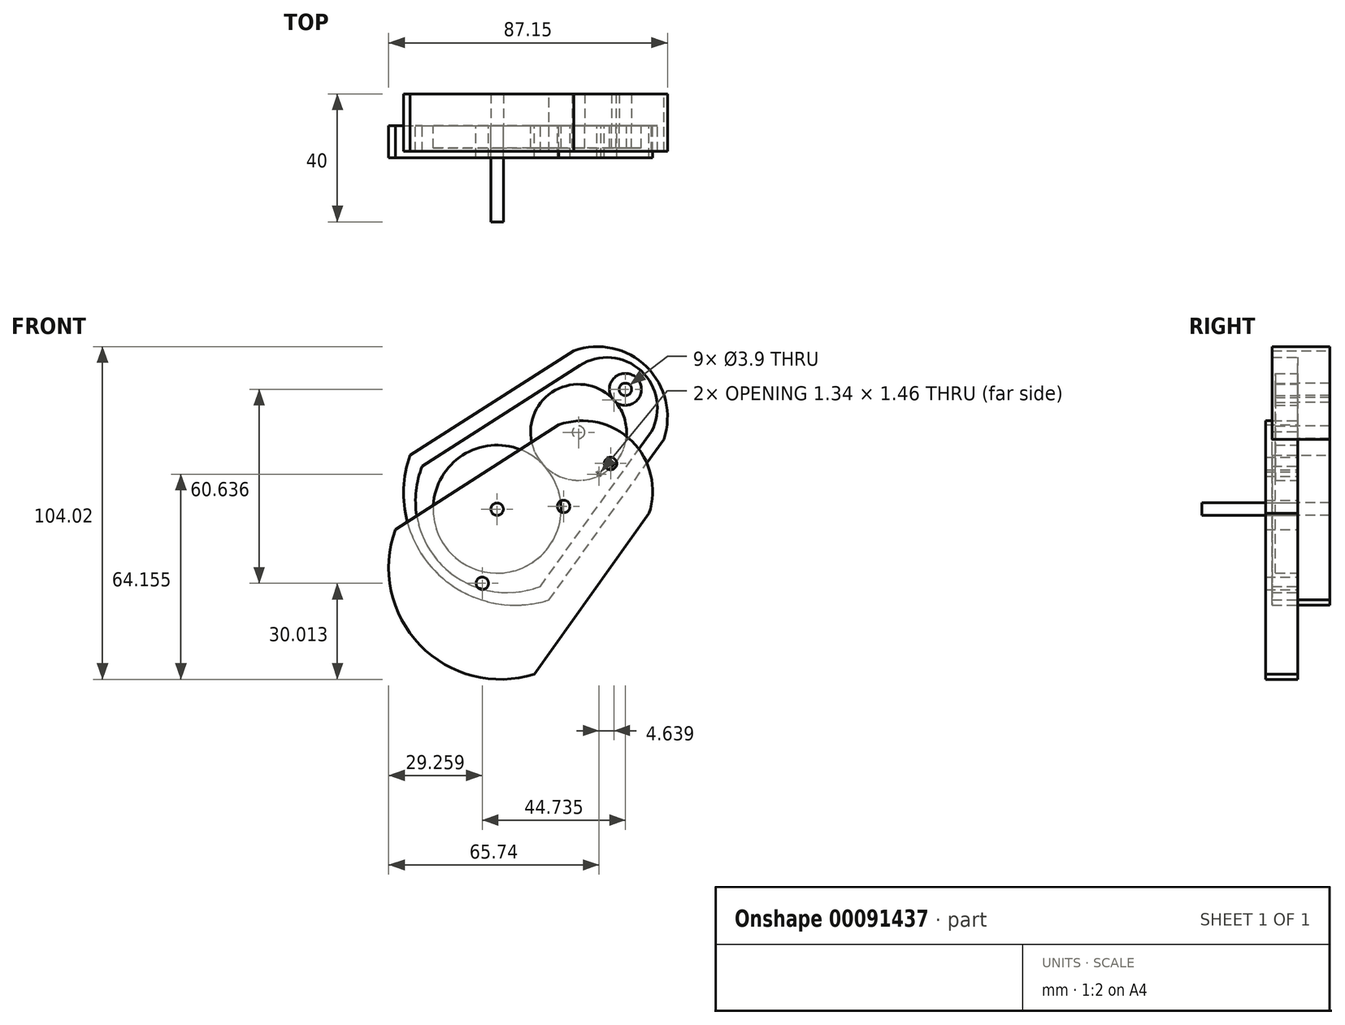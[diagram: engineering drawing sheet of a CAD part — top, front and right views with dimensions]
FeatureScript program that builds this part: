
annotation { "Feature Type Name" : "Feature", "Feature Type Description" : "" }
export const myFeature = defineFeature(function(context is Context, id is Id, definition is map)
    precondition{}
    {
        {
            var Q0;
            Q0=qCreatedBy(makeId("Front.planeOp"),FACE);
            var sketch = newSketch(context, id + "F0", { "sketchPlane" : qUnion([Q0])});
            skCircle(sketch, "E0", {"center": v(26.6, 43.79) * mm, "radius": 5 * mm});
            skCircle(sketch, "E1", {"center": v(11.94, 30.37) * mm, "radius": 15 * mm});
            skCircle(sketch, "E2", {"center": v(-13.5, 6.34) * mm, "radius": 20 * mm});
            skLineSegment(sketch, "E3", {"start": v(-36.89, 19.76) * mm, "end": v(12.3, 51.26) * mm});
            skLineSegment(sketch, "E4", {"start": v(0, -17.79) * mm, "end": v(34.74, 30.55) * mm});
            skArc(sketch, "E5", {"start": v(34.74, 30.55) * mm, "mid": v(31.52, 49.57) * mm, "end": v(12.3, 51.26) * mm});
            skArc(sketch, "E6", {"start": v(-36.89, 19.76) * mm, "mid": v(-30.8, -11.15) * mm, "end": v(0, -17.79) * mm});
            skCircle(sketch, "E7", {"center": v(-13.5, 6.34) * mm, "radius": 1.95 * mm});
            skCircle(sketch, "E8", {"center": v(11.94, 30.37) * mm, "radius": 1.95 * mm});
            skCircle(sketch, "E9", {"center": v(26.6, 43.79) * mm, "radius": 1.95 * mm});
            skLineSegment(sketch, "E10", {"start": v(-40.68, 23.15) * mm, "end": v(10.45, 55.9) * mm});
            skLineSegment(sketch, "E11", {"start": v(2.72, -22.05) * mm, "end": v(38.6, 28.17) * mm});
            skArc(sketch, "E12", {"start": v(38.6, 28.17) * mm, "mid": v(33.2, 50.84) * mm, "end": v(10.45, 55.9) * mm});
            skArc(sketch, "E13", {"start": v(-40.68, 23.15) * mm, "mid": v(-33.01, -12.93) * mm, "end": v(2.72, -22.05) * mm});
            skSolve(sketch);
        }
        {
            var Q0;
            Q0=makeQuery(id+"F0.imprint","IMPRINT",FACE,{"disambiguationData":[TD([[makeQuery(id+"F0.imprint","IMPRINT",EDGE,{"derivedFrom":sQuery(id+"F0.wireOp",EDGE,"E3")}),1.0]])]});
            extrude(context, id + "F1", {"entities" : qUnion([Q0]), "depth" : 8 * mm});
        }
        {
            var Q0;
            Q0 = qSketchRegion(id + "F0", true);
            var Q1;
            {var subQ0=sQuery(id+"F0.wireOp",EDGE,"E2");Q1=makeQuery(id+"F0.imprint","IMPRINT",FACE,{"disambiguationData":[TD([[makeQuery(id+"F0.imprint","IMPRINT",EDGE,{"derivedFrom":subQ0}),-1.0]])]});}
            var Q2;
            Q2=makeQuery(id+"F0.imprint","IMPRINT",FACE,{"disambiguationData":[TD([[makeQuery(id+"F0.imprint","IMPRINT",EDGE,{"derivedFrom":sQuery(id+"F0.wireOp",EDGE,"E8")}),-1.0]])]});
            var Q3;
            Q3=makeQuery(id+"F0.imprint","IMPRINT",FACE,{"disambiguationData":[TD([[makeQuery(id+"F0.imprint","IMPRINT",EDGE,{"derivedFrom":sQuery(id+"F0.wireOp",EDGE,"E2")}),1.0]])]});
            var Q4;
            Q4=makeQuery(id+"F0.imprint","IMPRINT",FACE,{"disambiguationData":[TD([[makeQuery(id+"F0.imprint","IMPRINT",EDGE,{"derivedFrom":sQuery(id+"F0.wireOp",EDGE,"E9")}),-1.0]])]});
            extrude(context, id + "F2", {"entities" : qUnion([Q0, Q1, Q2, Q3, Q4]), "operationType" : NewBodyOperationType.ADD, "oppositeDirection" : true, "depth" : 10 * mm});
        }
        {
            var Q0;
            Q0=qCreatedBy(makeId("Front.planeOp"),FACE);
            var sketch = newSketch(context, id + "F3", { "sketchPlane" : qUnion([Q0])});
            skCircle(sketch, "E14", {"center": v(21.95, 20.6) * mm, "radius": 5 * mm});
            skCircle(sketch, "E15", {"center": v(7.3, 7.18) * mm, "radius": 15 * mm});
            skCircle(sketch, "E16", {"center": v(-18.14, -16.85) * mm, "radius": 20 * mm});
            skLineSegment(sketch, "E17", {"start": v(-41.53, -3.43) * mm, "end": v(7.67, 28.08) * mm});
            skLineSegment(sketch, "E18", {"start": v(-4.64, -40.97) * mm, "end": v(30.1, 7.36) * mm});
            skArc(sketch, "E19", {"start": v(30.1, 7.36) * mm, "mid": v(26.88, 26.38) * mm, "end": v(7.67, 28.08) * mm});
            skArc(sketch, "E20", {"start": v(-41.53, -3.43) * mm, "mid": v(-35.44, -34.34) * mm, "end": v(-4.64, -40.97) * mm});
            skCircle(sketch, "E21", {"center": v(-18.14, -16.85) * mm, "radius": 1.95 * mm});
            skCircle(sketch, "E22", {"center": v(7.3, 7.18) * mm, "radius": 1.95 * mm});
            skCircle(sketch, "E23", {"center": v(21.95, 20.6) * mm, "radius": 1.95 * mm});
            skLineSegment(sketch, "E24", {"start": v(-45.32, -0.04) * mm, "end": v(5.81, 32.7) * mm});
            skLineSegment(sketch, "E25", {"start": v(-1.92, -45.24) * mm, "end": v(33.96, 4.99) * mm});
            skArc(sketch, "E26", {"start": v(33.96, 4.99) * mm, "mid": v(28.56, 27.66) * mm, "end": v(5.81, 32.7) * mm});
            skArc(sketch, "E27", {"start": v(-45.32, -0.04) * mm, "mid": v(-37.65, -36.11) * mm, "end": v(-1.92, -45.24) * mm});
            skSolve(sketch);
        }
        {
            var Q0;
            Q0=makeQuery(id+"F3.imprint","IMPRINT",FACE,{"disambiguationData":[TD([[makeQuery(id+"F3.imprint","IMPRINT",EDGE,{"derivedFrom":sQuery(id+"F3.wireOp",EDGE,"E17")}),1.0]])]});
            var Q1;
            {var subQ0=sQuery(id+"F3.wireOp",EDGE,"E16");Q1=makeQuery(id+"F3.imprint","IMPRINT",FACE,{"disambiguationData":[TD([[makeQuery(id+"F3.imprint","IMPRINT",EDGE,{"derivedFrom":subQ0}),-1.0]])]});}
            var Q2;
            Q2=makeQuery(id+"F3.imprint","IMPRINT",FACE,{"disambiguationData":[TD([[makeQuery(id+"F3.imprint","IMPRINT",EDGE,{"derivedFrom":sQuery(id+"F3.wireOp",EDGE,"E16")}),1.0]])]});
            var Q3;
            Q3=makeQuery(id+"F3.imprint","IMPRINT",FACE,{"disambiguationData":[TD([[makeQuery(id+"F3.imprint","IMPRINT",EDGE,{"derivedFrom":sQuery(id+"F3.wireOp",EDGE,"E22")}),-1.0]])]});
            var Q4;
            Q4=makeQuery(id+"F3.imprint","IMPRINT",FACE,{"disambiguationData":[TD([[makeQuery(id+"F3.imprint","IMPRINT",EDGE,{"derivedFrom":sQuery(id+"F3.wireOp",EDGE,"E23")}),-1.0]])]});
            extrude(context, id + "F4", {"entities" : qUnion([Q0, Q1, Q2, Q3, Q4]), "depth" : 10 * mm});
        }
        {
            var Q0;
            Q0=makeQuery(id+"F0.imprint","IMPRINT",FACE,{"disambiguationData":[TD([[makeQuery(id+"F0.imprint","IMPRINT",EDGE,{"derivedFrom":sQuery(id+"F0.wireOp",EDGE,"E7")}),1.0]])]});
            extrude(context, id + "F5", {"entities" : qUnion([Q0]), "depth" : 30 * mm});
        }
        {
            var Q0;
            Q0=makeQuery(id+"F0.imprint","IMPRINT",FACE,{"disambiguationData":[TD([[makeQuery(id+"F0.imprint","IMPRINT",EDGE,{"derivedFrom":sQuery(id+"F0.wireOp",EDGE,"E2")}),1.0]])]});
            extrude(context, id + "F6", {"entities" : qUnion([Q0]), "depth" : 7 * mm});
        }
        {
            var Q0;
            Q0=makeQuery(id+"F0.imprint","IMPRINT",FACE,{"disambiguationData":[TD([[makeQuery(id+"F0.imprint","IMPRINT",EDGE,{"derivedFrom":sQuery(id+"F0.wireOp",EDGE,"E8")}),-1.0]])]});
            extrude(context, id + "F7", {"entities" : qUnion([Q0]), "depth" : 7 * mm});
        }
        {
            var Q0;
            Q0=makeQuery(id+"F0.imprint","IMPRINT",FACE,{"disambiguationData":[TD([[makeQuery(id+"F0.imprint","IMPRINT",EDGE,{"derivedFrom":sQuery(id+"F0.wireOp",EDGE,"E9")}),-1.0]])]});
            extrude(context, id + "F8", {"entities" : qUnion([Q0]), "depth" : 7 * mm});
        }
    });
